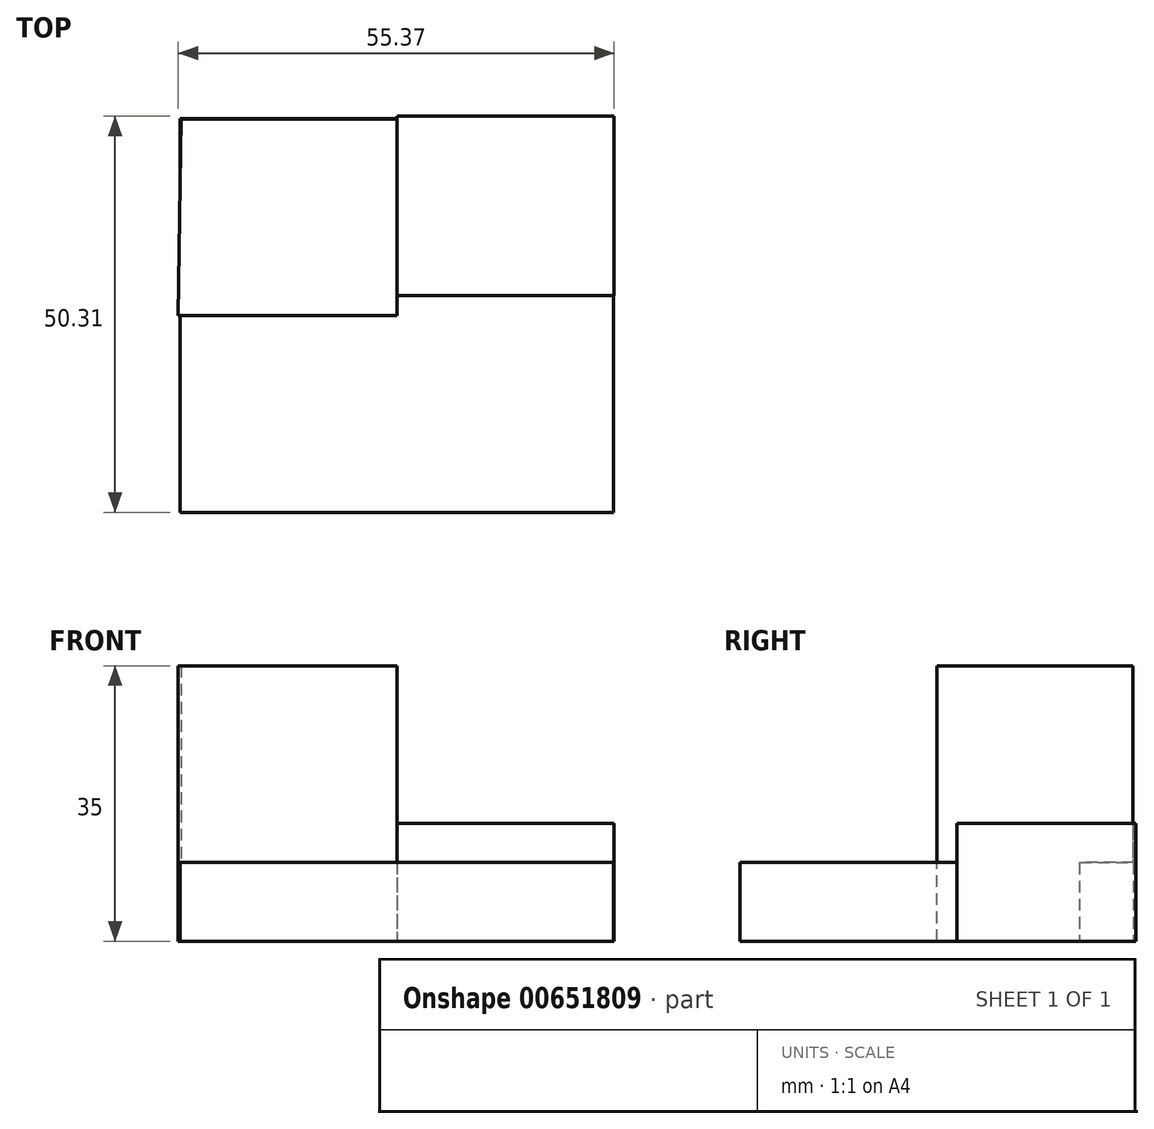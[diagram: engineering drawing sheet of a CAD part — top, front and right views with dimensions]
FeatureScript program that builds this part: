
annotation { "Feature Type Name" : "Feature", "Feature Type Description" : "" }
export const myFeature = defineFeature(function(context is Context, id is Id, definition is map)
    precondition{}
    {
        {
            var Q0;
            Q0=qCreatedBy(makeId("Top.planeOp"),FACE);
            var sketch = newSketch(context, id + "F0", { "sketchPlane" : qUnion([Q0])});
            skLineSegment(sketch, "E0.bottom", {"start": v(-27.5, 25) * mm, "end": v(27.5, 25) * mm});
            skLineSegment(sketch, "E0.top", {"start": v(-27.5, -25) * mm, "end": v(27.5, -25) * mm});
            skLineSegment(sketch, "E0.left", {"start": v(-27.5, 25) * mm, "end": v(-27.5, -25) * mm});
            skLineSegment(sketch, "E0.right", {"start": v(27.5, 25) * mm, "end": v(27.5, -25) * mm});
            skPoint(sketch, "E0.middle", {"position": v(0, 0) * mm});
            skSolve(sketch);
        }
        {
            var Q0;
            Q0 = qSketchRegion(id + "F0", true);
            extrude(context, id + "F1", {"entities" : qUnion([Q0]), "depth" : 10 * mm, "offsetDistance" : 25.4 * mm});
        }
        {
            var Q0;
            Q0=qCreatedBy(makeId("Top.planeOp"),FACE);
            var sketch = newSketch(context, id + "F2", { "sketchPlane" : qUnion([Q0])});
            skLineSegment(sketch, "E1", {"start": v(-27.78, 0) * mm, "end": v(0, 0) * mm});
            skLineSegment(sketch, "E2", {"start": v(0, 0) * mm, "end": v(0, 24.93) * mm});
            skLineSegment(sketch, "E3", {"start": v(0, 24.93) * mm, "end": v(-27.4, 24.93) * mm});
            skLineSegment(sketch, "E4", {"start": v(-27.4, 24.93) * mm, "end": v(-27.78, 0) * mm});
            skSolve(sketch);
        }
        {
            var Q0;
            Q0 = qSketchRegion(id + "F2", true);
            extrude(context, id + "F3", {"entities" : qUnion([Q0]), "operationType" : NewBodyOperationType.ADD, "depth" : 35 * mm, "offsetDistance" : 25.4 * mm});
        }
        {
            var Q0;
            Q0=qCreatedBy(makeId("Top.planeOp"),FACE);
            var sketch = newSketch(context, id + "F4", { "sketchPlane" : qUnion([Q0])});
            skLineSegment(sketch, "E5", {"start": v(0, 2.56) * mm, "end": v(27.59, 2.56) * mm});
            skLineSegment(sketch, "E6", {"start": v(27.59, 2.56) * mm, "end": v(27.59, 25.31) * mm});
            skLineSegment(sketch, "E7", {"start": v(27.59, 25.31) * mm, "end": v(0, 25.31) * mm});
            skLineSegment(sketch, "E8", {"start": v(0, 25.31) * mm, "end": v(0, 2.56) * mm});
            skSolve(sketch);
        }
        {
            var Q0;
            Q0 = qSketchRegion(id + "F4", true);
            extrude(context, id + "F5", {"entities" : qUnion([Q0]), "operationType" : NewBodyOperationType.ADD, "depth" : 15 * mm, "offsetDistance" : 25.4 * mm});
        }
    });
